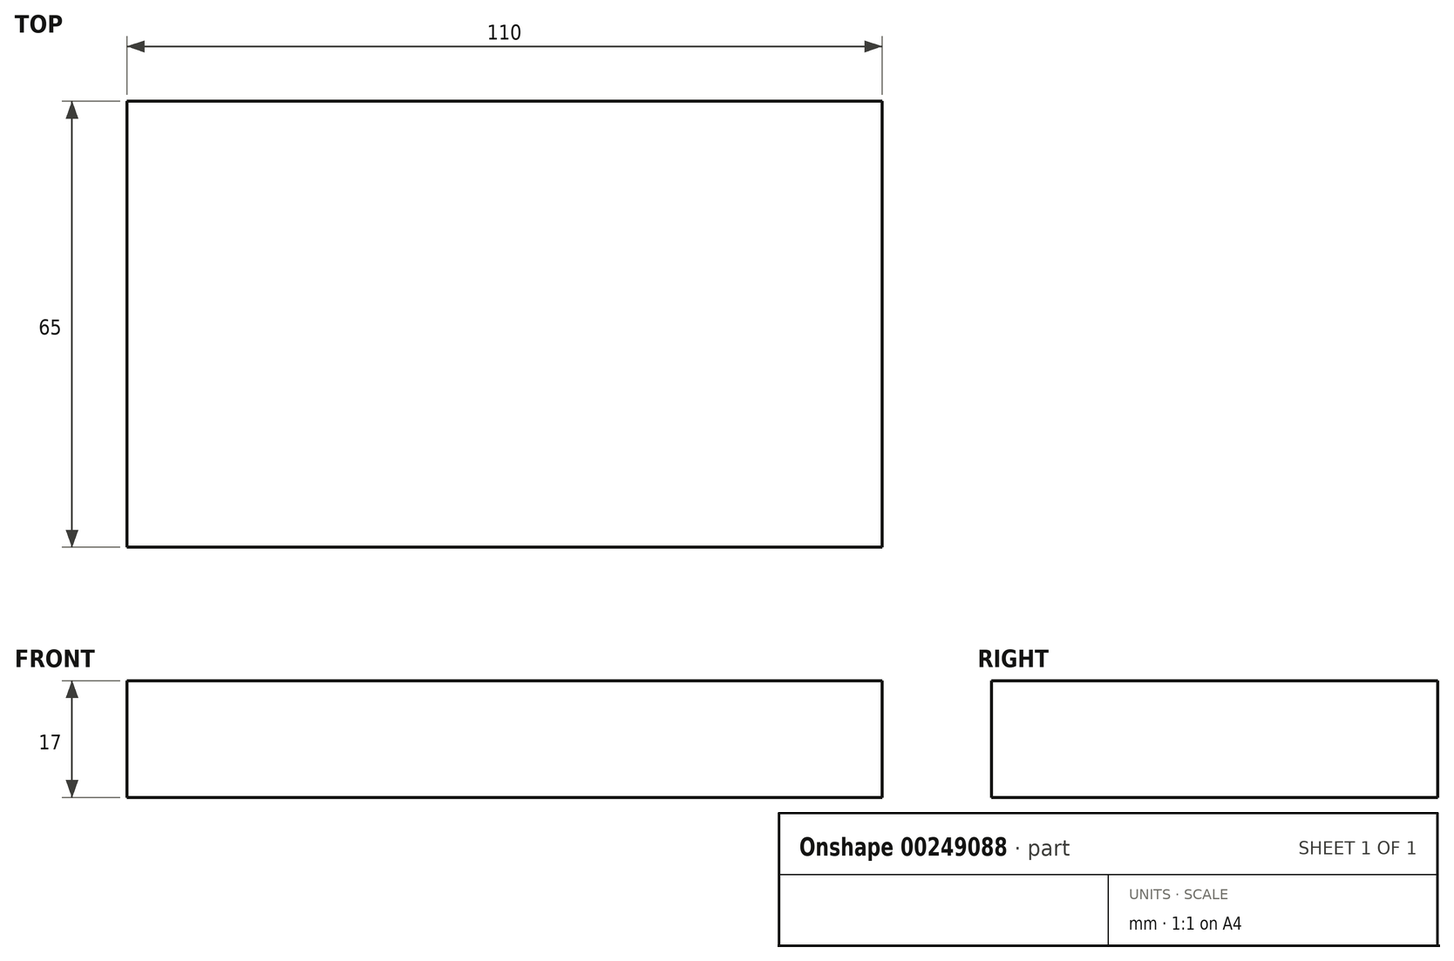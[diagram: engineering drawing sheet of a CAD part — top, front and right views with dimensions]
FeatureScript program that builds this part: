
annotation { "Feature Type Name" : "Feature", "Feature Type Description" : "" }
export const myFeature = defineFeature(function(context is Context, id is Id, definition is map)
    precondition{}
    {
        {
            var Q0;
            Q0=qCreatedBy(makeId("Top.planeOp"),FACE);
            var sketch = newSketch(context, id + "F0", { "sketchPlane" : qUnion([Q0])});
            skLineSegment(sketch, "E0.bottom", {"start": v(-55, 32.5) * mm, "end": v(55, 32.5) * mm});
            skLineSegment(sketch, "E0.top", {"start": v(-55, -32.5) * mm, "end": v(55, -32.5) * mm});
            skLineSegment(sketch, "E0.left", {"start": v(-55, 32.5) * mm, "end": v(-55, -32.5) * mm});
            skLineSegment(sketch, "E0.right", {"start": v(55, 32.5) * mm, "end": v(55, -32.5) * mm});
            skPoint(sketch, "E1", {"position": v(0, 32.5) * mm});
            skPoint(sketch, "E2", {"position": v(-55, 0) * mm});
            skSolve(sketch);
        }
        {
            var Q0;
            Q0=makeQuery(id+"F0.imprint","IMPRINT",FACE,{"disambiguationData":[TD([[makeQuery(id+"F0.imprint","IMPRINT",EDGE,{"derivedFrom":sQuery(id+"F0.wireOp",EDGE,"E0.bottom")}),-1.0]])]});
            extrude(context, id + "F1", {"entities" : qUnion([Q0]), "oppositeDirection" : true, "depth" : 17 * mm});
        }
    });
